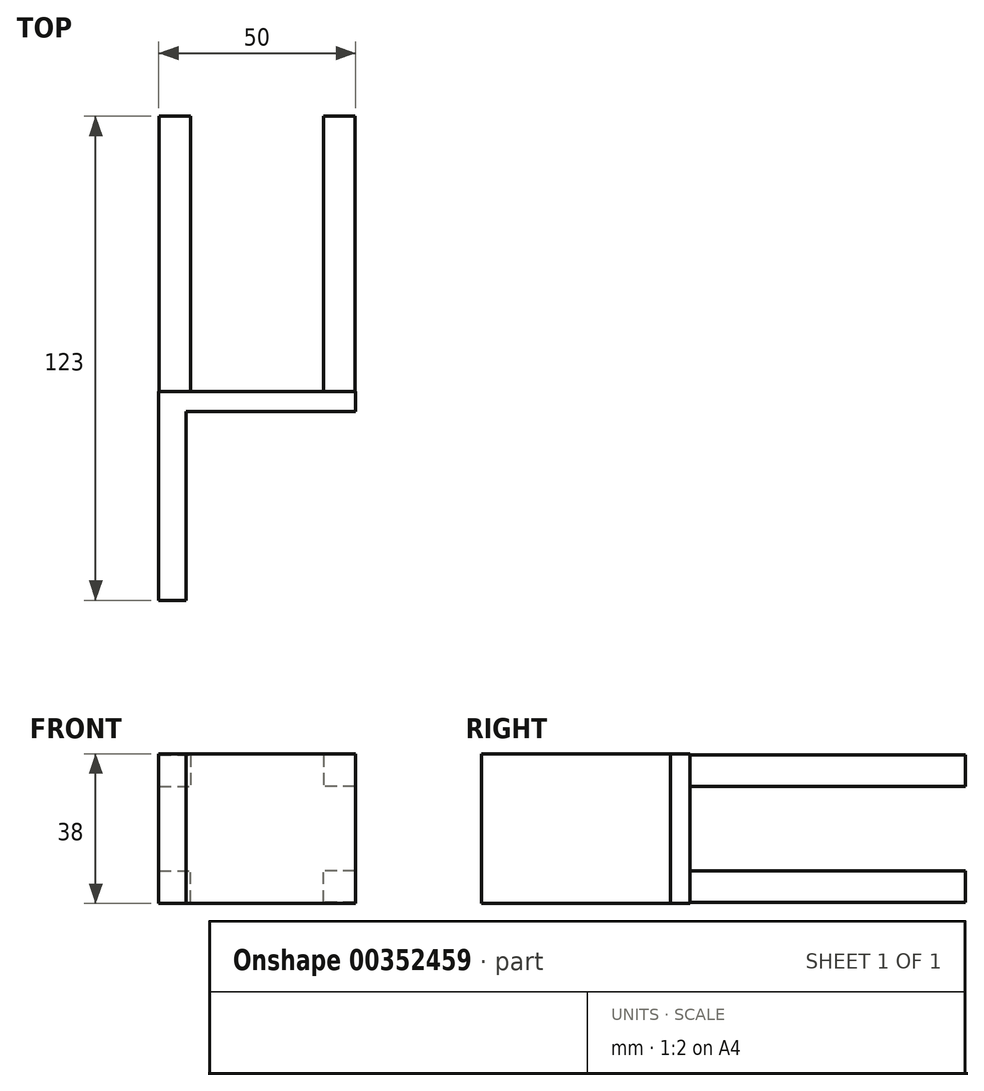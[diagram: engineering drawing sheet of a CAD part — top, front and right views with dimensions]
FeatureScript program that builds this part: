
annotation { "Feature Type Name" : "Feature", "Feature Type Description" : "" }
export const myFeature = defineFeature(function(context is Context, id is Id, definition is map)
    precondition{}
    {
        {
            var Q0;
            Q0=qCreatedBy(makeId("Front.planeOp"),FACE);
            var sketch = newSketch(context, id + "F0", { "sketchPlane" : qUnion([Q0])});
            skLineSegment(sketch, "E0.bottom", {"start": v(-25, 19) * mm, "end": v(25, 19) * mm});
            skLineSegment(sketch, "E0.top", {"start": v(-25, -19) * mm, "end": v(25, -19) * mm});
            skLineSegment(sketch, "E0.left", {"start": v(-25, 19) * mm, "end": v(-25, -19) * mm});
            skLineSegment(sketch, "E0.right", {"start": v(25, 19) * mm, "end": v(25, -19) * mm});
            skPoint(sketch, "E0.middle", {"position": v(0, 0) * mm});
            skSolve(sketch);
        }
        {
            var Q0;
            Q0 = qSketchRegion(id + "F0", true);
            extrude(context, id + "F1", {"entities" : qUnion([Q0]), "depth" : 5 * mm});
        }
        {
            var Q0;
            Q0=qCreatedBy(makeId("Front.planeOp"),FACE);
            var sketch = newSketch(context, id + "F2", { "sketchPlane" : qUnion([Q0])});
            skLineSegment(sketch, "E1.bottom", {"start": v(24.86, 18.72) * mm, "end": v(16.86, 18.72) * mm});
            skLineSegment(sketch, "E1.top", {"start": v(24.86, 10.72) * mm, "end": v(16.86, 10.72) * mm});
            skLineSegment(sketch, "E1.left", {"start": v(24.86, 18.72) * mm, "end": v(24.86, 10.72) * mm});
            skLineSegment(sketch, "E1.right", {"start": v(16.86, 18.72) * mm, "end": v(16.86, 10.72) * mm});
            skLineSegment(sketch, "E2.MirrorCS", {"start": v(24.86, -18.72) * mm, "end": v(16.86, -18.72) * mm});
            skLineSegment(sketch, "E3.MirrorCS", {"start": v(24.86, -10.72) * mm, "end": v(16.86, -10.72) * mm});
            skLineSegment(sketch, "E4.MirrorCS", {"start": v(16.86, -18.72) * mm, "end": v(16.86, -10.72) * mm});
            skLineSegment(sketch, "E5.MirrorCS", {"start": v(24.86, -18.72) * mm, "end": v(24.86, -10.72) * mm});
            skLineSegment(sketch, "E6.MirrorCS", {"start": v(-16.86, -18.72) * mm, "end": v(-16.86, -10.72) * mm});
            skLineSegment(sketch, "E7.MirrorCS", {"start": v(-24.86, -10.72) * mm, "end": v(-16.86, -10.72) * mm});
            skLineSegment(sketch, "E8.MirrorCS", {"start": v(-24.86, -18.72) * mm, "end": v(-16.86, -18.72) * mm});
            skLineSegment(sketch, "E9.MirrorCS", {"start": v(-16.86, 18.72) * mm, "end": v(-16.86, 10.72) * mm});
            skLineSegment(sketch, "E10.MirrorCS", {"start": v(-24.86, 18.72) * mm, "end": v(-24.86, 10.72) * mm});
            skLineSegment(sketch, "E11.MirrorCS", {"start": v(-24.86, 10.72) * mm, "end": v(-16.86, 10.72) * mm});
            skLineSegment(sketch, "E12.MirrorCS", {"start": v(-24.86, -18.72) * mm, "end": v(-24.86, -10.72) * mm});
            skLineSegment(sketch, "E13.MirrorCS", {"start": v(-24.86, 18.72) * mm, "end": v(-16.86, 18.72) * mm});
            skSolve(sketch);
        }
        {
            var Q0;
            Q0 = qSketchRegion(id + "F2", true);
            extrude(context, id + "F3", {"entities" : qUnion([Q0]), "operationType" : NewBodyOperationType.ADD, "oppositeDirection" : true, "depth" : 70 * mm});
        }
        {
            var Q0;
            Q0=makeQuery(id+"F1.opExtrude","SWEPT_FACE",FACE,{"disambiguationData":[OSD([sQuery(id+"F0.wireOp",EDGE,"E0.left")])]});
            var sketch = newSketch(context, id + "F4", { "sketchPlane" : qUnion([Q0])});
            skLineSegment(sketch, "E14.bottom", {"start": v(5, 19) * mm, "end": v(53, 19) * mm});
            skLineSegment(sketch, "E14.top", {"start": v(5, -19) * mm, "end": v(53, -19) * mm});
            skLineSegment(sketch, "E14.left", {"start": v(5, 19) * mm, "end": v(5, -19) * mm});
            skLineSegment(sketch, "E14.right", {"start": v(53, 19) * mm, "end": v(53, -19) * mm});
            skSolve(sketch);
        }
        {
            var Q0;
            Q0=makeQuery(id+"F4.imprint","IMPRINT",FACE,{"disambiguationData":[TD([[makeQuery(id+"F4.imprint","IMPRINT",EDGE,{"derivedFrom":sQuery(id+"F4.wireOp",EDGE,"E14.bottom")}),-1.0]])]});
            extrude(context, id + "F5", {"entities" : qUnion([Q0]), "operationType" : NewBodyOperationType.ADD, "oppositeDirection" : true, "depth" : 7 * mm});
        }
    });
